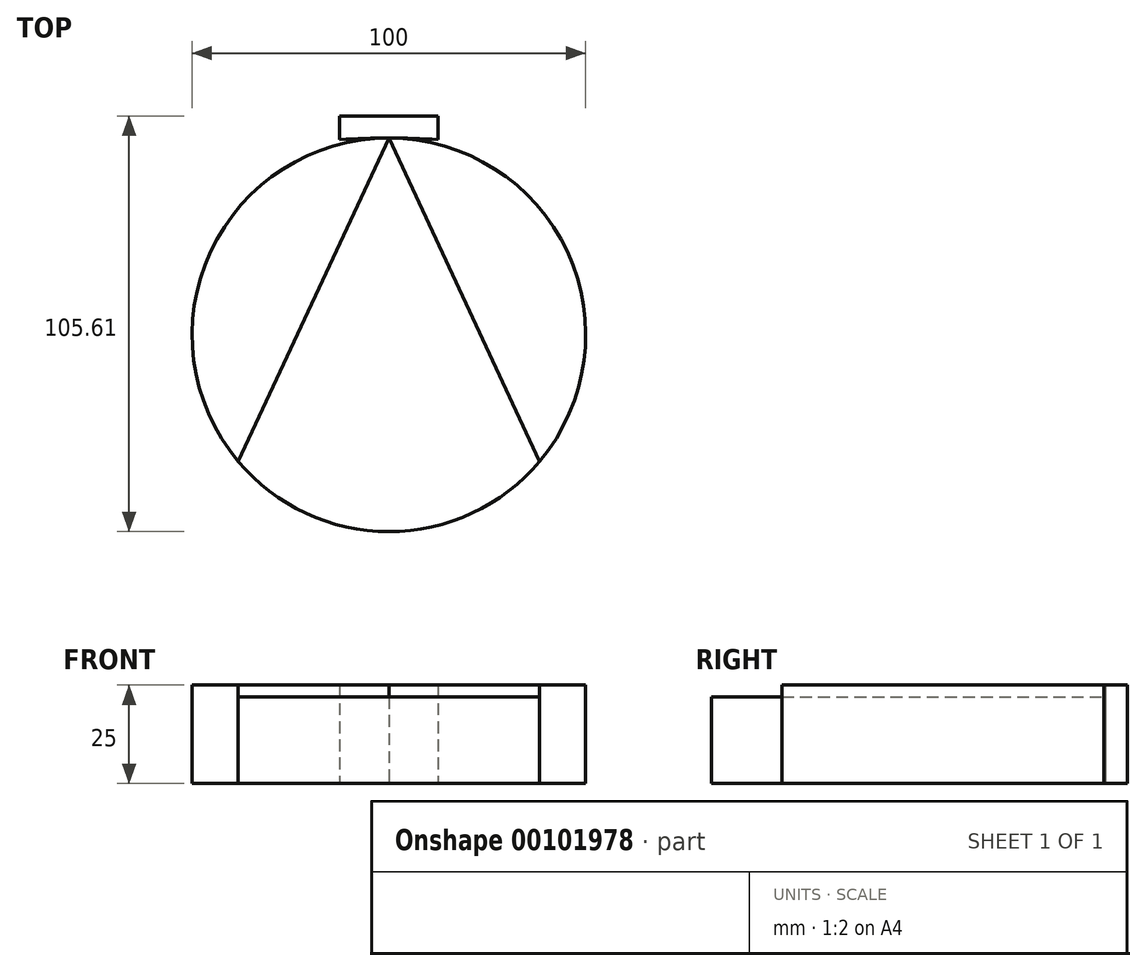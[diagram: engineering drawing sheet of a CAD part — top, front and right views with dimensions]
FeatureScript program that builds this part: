
annotation { "Feature Type Name" : "Feature", "Feature Type Description" : "" }
export const myFeature = defineFeature(function(context is Context, id is Id, definition is map)
    precondition{}
    {
        {
            var Q0;
            Q0=qCreatedBy(makeId("Top.planeOp"),FACE);
            var sketch = newSketch(context, id + "F0", { "sketchPlane" : qUnion([Q0])});
            skCircle(sketch, "E0", {"center": v(0, 0) * mm, "radius": 50 * mm});
            skArc(sketch, "E1", {"start": v(12.5, 49.6) * mm, "mid": v(0, 50) * mm, "end": v(-12.5, 49.6) * mm});
            skPoint(sketch, "E2", {"position": v(0, 50) * mm});
            skLineSegment(sketch, "E3", {"start": v(-12.5, 49.6) * mm, "end": v(-12.5, 55.6) * mm});
            skLineSegment(sketch, "E4", {"start": v(-12.5, 55.6) * mm, "end": v(12.5, 55.6) * mm});
            skLineSegment(sketch, "E5", {"start": v(12.5, 55.6) * mm, "end": v(12.5, 49.6) * mm});
            skPoint(sketch, "E6", {"position": v(38.3, -32.14) * mm});
            skPoint(sketch, "E7", {"position": v(-38.3, -32.14) * mm});
            skLineSegment(sketch, "E8", {"start": v(38.3, -32.14) * mm, "end": v(0, 50) * mm});
            skLineSegment(sketch, "E9", {"start": v(-38.3, -32.14) * mm, "end": v(0, 50) * mm});
            skLineSegment(sketch, "E10", {"start": v(0, 0) * mm, "end": v(0, 50) * mm, "construction": true});
            skSolve(sketch);
        }
        {
            var Q0;
            {var subQ0=sQuery(id+"F0.wireOp",EDGE,"E9");Q0=makeQuery(id+"F0.imprint","IMPRINT",FACE,{"disambiguationData":[TD([[makeQuery(id+"F0.imprint","IMPRINT",EDGE,{"derivedFrom":subQ0}),1.0]])]});}
            var Q1;
            {var subQ0=sQuery(id+"F0.wireOp",EDGE,"E8");Q1=makeQuery(id+"F0.imprint","IMPRINT",FACE,{"disambiguationData":[TD([[makeQuery(id+"F0.imprint","IMPRINT",EDGE,{"derivedFrom":subQ0}),-1.0]])]});}
            var Q2;
            {var subQ0=sQuery(id+"F0.wireOp",EDGE,"E3");Q2=makeQuery(id+"F0.imprint","IMPRINT",FACE,{"disambiguationData":[TD([[makeQuery(id+"F0.imprint","IMPRINT",EDGE,{"derivedFrom":subQ0}),-1.0]])]});}
            extrude(context, id + "F1", {"entities" : qUnion([Q0, Q1, Q2]), "depth" : 25 * mm});
        }
        {
            var Q0;
            {var subQ0=sQuery(id+"F0.wireOp",EDGE,"E8");Q0=makeQuery(id+"F0.imprint","IMPRINT",FACE,{"disambiguationData":[TD([[makeQuery(id+"F0.imprint","IMPRINT",EDGE,{"derivedFrom":subQ0}),1.0]])]});}
            extrude(context, id + "F2", {"entities" : qUnion([Q0]), "depth" : 22 * mm});
        }
    });
